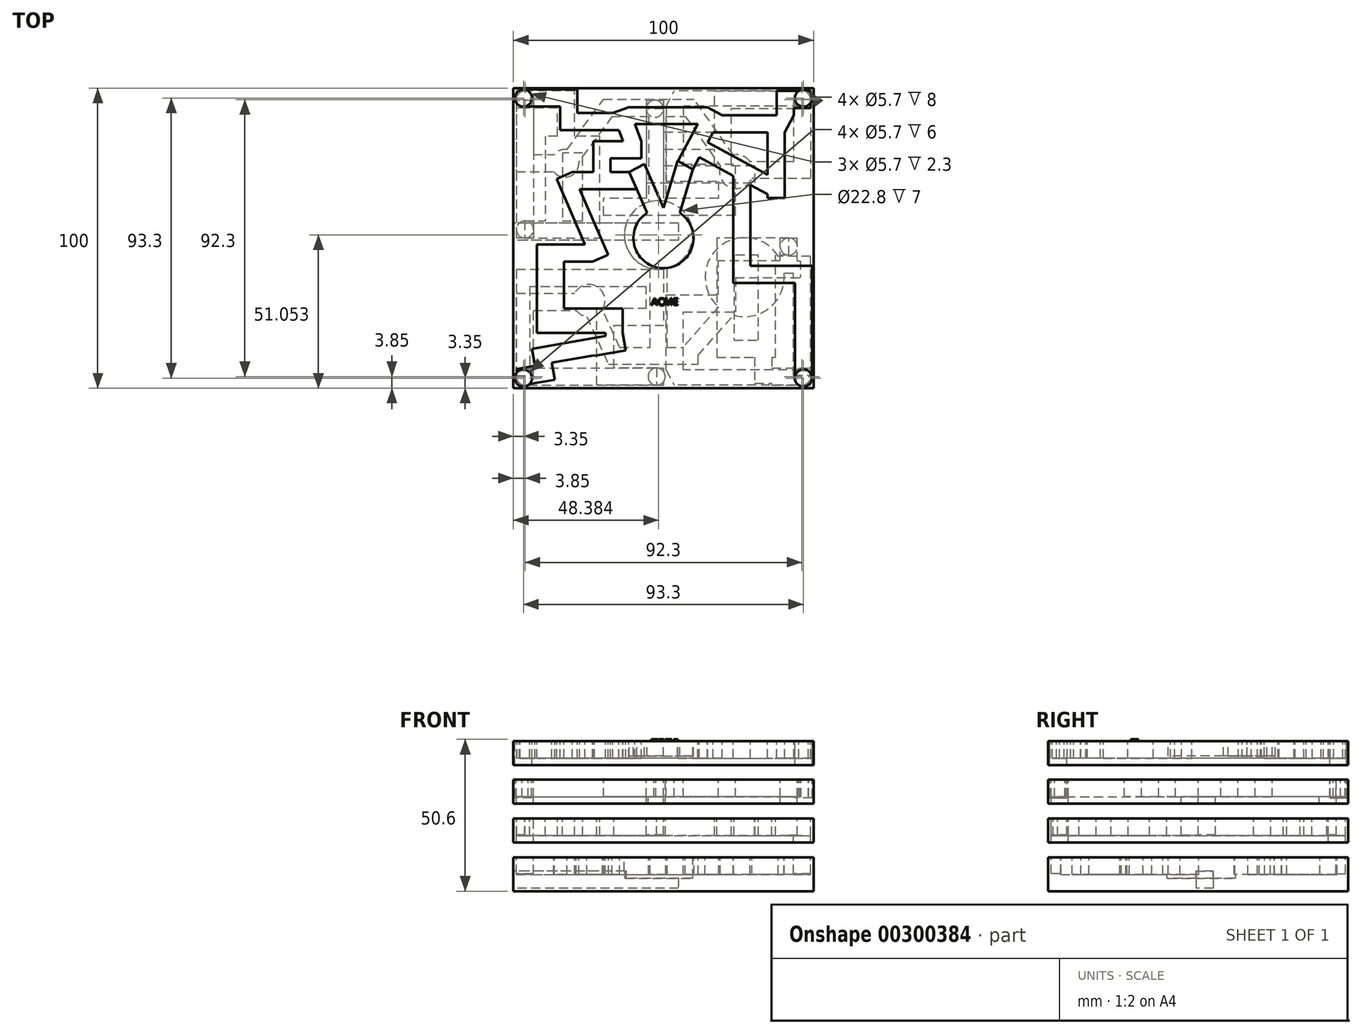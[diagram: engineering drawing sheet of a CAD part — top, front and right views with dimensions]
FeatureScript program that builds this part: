
annotation { "Feature Type Name" : "Feature", "Feature Type Description" : "" }
export const myFeature = defineFeature(function(context is Context, id is Id, definition is map)
    precondition{}
    {
        {
            var Q0;
            Q0=qCreatedBy(makeId("Top.planeOp"),FACE);
            var sketch = newSketch(context, id + "F0", { "sketchPlane" : qUnion([Q0])});
            skLineSegment(sketch, "E0.bottom", {"start": v(-50, 50) * mm, "end": v(50, 50) * mm});
            skLineSegment(sketch, "E0.top", {"start": v(-50, -50) * mm, "end": v(50, -50) * mm});
            skLineSegment(sketch, "E0.left", {"start": v(-50, 50) * mm, "end": v(-50, -50) * mm});
            skLineSegment(sketch, "E0.right", {"start": v(50, 50) * mm, "end": v(50, -50) * mm});
            skPoint(sketch, "E0.middle", {"position": v(0, 0) * mm});
            skSolve(sketch);
        }
        {
            var Q0;
            Q0=qSketchRegion(id+"F0",true);
            extrude(context, id + "F1", {"entities" : qUnion([Q0]), "oppositeDirection" : true, "depth" : 50 * mm});
        }
        {
            var Q0;
            Q0=makeQuery(id+"F1.opExtrude","CAP_FACE",FACE,{"disambiguationData":[OSD([sQuery(id+"F0.wireOp",EDGE,"E0.bottom"),sQuery(id+"F0.wireOp",EDGE,"E0.top"),sQuery(id+"F0.wireOp",EDGE,"E0.left"),sQuery(id+"F0.wireOp",EDGE,"E0.right")])],"isStart":true});
            var sketch = newSketch(context, id + "F2", { "sketchPlane" : qUnion([Q0])});
            skCircle(sketch, "E1", {"center": v(0, 0) * mm, "radius": 10 * mm});
            skSolve(sketch);
        }
        {
            var Q0;
            Q0=qSketchRegion(id+"F2",true);
            extrude(context, id + "F3", {"entities" : qUnion([Q0]), "operationType" : NewBodyOperationType.REMOVE, "oppositeDirection" : true, "depth" : 5 * mm});
        }
        {
            var Q0;
            Q0=makeQuery(id+"F1.opExtrude","CAP_FACE",FACE,{"disambiguationData":[OSD([sQuery(id+"F0.wireOp",EDGE,"E0.bottom"),sQuery(id+"F0.wireOp",EDGE,"E0.top"),sQuery(id+"F0.wireOp",EDGE,"E0.left"),sQuery(id+"F0.wireOp",EDGE,"E0.right")])],"isStart":true});
            var sketch = newSketch(context, id + "F4", { "sketchPlane" : qUnion([Q0])});
            skLineSegment(sketch, "E2", {"start": v(0, 10) * mm, "end": v(-6.36, 24.68) * mm});
            skLineSegment(sketch, "E3", {"start": v(0, 10) * mm, "end": v(4.66, 25.69) * mm});
            skLineSegment(sketch, "E4", {"start": v(4.66, 25.69) * mm, "end": v(9.78, 22.9) * mm});
            skLineSegment(sketch, "E5", {"start": v(9.78, 22.9) * mm, "end": v(5.46, 8.38) * mm});
            skLineSegment(sketch, "E6", {"start": v(5.46, 8.38) * mm, "end": v(0, 10) * mm});
            skLineSegment(sketch, "E7", {"start": v(-6.36, 24.68) * mm, "end": v(-11.36, 21.94) * mm});
            skLineSegment(sketch, "E8", {"start": v(-11.36, 21.94) * mm, "end": v(-5.46, 8.38) * mm});
            skLineSegment(sketch, "E9", {"start": v(-5.46, 8.38) * mm, "end": v(0, 10) * mm});
            skSolve(sketch);
        }
        {
            var Q0;
            Q0=qSketchRegion(id+"F4",true);
            extrude(context, id + "F5", {"entities" : qUnion([Q0]), "operationType" : NewBodyOperationType.REMOVE, "oppositeDirection" : true, "depth" : 5 * mm});
        }
        {
            var Q0;
            Q0=makeQuery(id+"F1.opExtrude","CAP_FACE",FACE,{"disambiguationData":[OSD([sQuery(id+"F0.wireOp",EDGE,"E0.bottom"),sQuery(id+"F0.wireOp",EDGE,"E0.top"),sQuery(id+"F0.wireOp",EDGE,"E0.left"),sQuery(id+"F0.wireOp",EDGE,"E0.right")])],"isStart":true});
            var sketch = newSketch(context, id + "F6", { "sketchPlane" : qUnion([Q0])});
            skLineSegment(sketch, "E10.bottom", {"start": v(-11.36, 21.94) * mm, "end": v(-30.36, 21.94) * mm});
            skLineSegment(sketch, "E10.top", {"start": v(-8.88, 16.24) * mm, "end": v(-27.88, 16.24) * mm});
            skLineSegment(sketch, "E10.left", {"start": v(-11.36, 21.94) * mm, "end": v(-8.88, 16.24) * mm});
            skLineSegment(sketch, "E10.right", {"start": v(-30.36, 21.94) * mm, "end": v(-27.88, 16.24) * mm});
            skLineSegment(sketch, "E11.bottom", {"start": v(-23.36, 21.94) * mm, "end": v(-17.66, 21.94) * mm});
            skLineSegment(sketch, "E11.top", {"start": v(-23.36, 32.25) * mm, "end": v(-17.66, 32.25) * mm});
            skLineSegment(sketch, "E11.left", {"start": v(-23.36, 21.94) * mm, "end": v(-23.36, 32.25) * mm});
            skLineSegment(sketch, "E11.right", {"start": v(-17.66, 21.94) * mm, "end": v(-17.66, 32.25) * mm});
            skLineSegment(sketch, "E12.bottom", {"start": v(-17.66, 32.25) * mm, "end": v(-7.41, 32.25) * mm});
            skLineSegment(sketch, "E12.top", {"start": v(-17.66, 26.55) * mm, "end": v(-7.41, 26.55) * mm});
            skLineSegment(sketch, "E12.left", {"start": v(-17.66, 32.25) * mm, "end": v(-17.66, 26.55) * mm});
            skLineSegment(sketch, "E12.right", {"start": v(-7.41, 32.25) * mm, "end": v(-7.41, 26.55) * mm});
            skLineSegment(sketch, "E13.bottom", {"start": v(-7.41, 32.25) * mm, "end": v(-12.77, 30.3) * mm});
            skLineSegment(sketch, "E13.top", {"start": v(-11.56, 43.65) * mm, "end": v(-16.92, 41.7) * mm});
            skLineSegment(sketch, "E13.left", {"start": v(-7.41, 32.25) * mm, "end": v(-11.56, 43.65) * mm});
            skLineSegment(sketch, "E13.right", {"start": v(-12.77, 30.3) * mm, "end": v(-16.92, 41.7) * mm});
            skLineSegment(sketch, "E14.bottom", {"start": v(-16.92, 41.7) * mm, "end": v(-31.14, 41.7) * mm});
            skLineSegment(sketch, "E14.top", {"start": v(-14.84, 36) * mm, "end": v(-29.06, 36) * mm});
            skLineSegment(sketch, "E14.left", {"start": v(-16.92, 41.7) * mm, "end": v(-14.84, 36) * mm});
            skLineSegment(sketch, "E14.right", {"start": v(-31.14, 41.7) * mm, "end": v(-29.06, 36) * mm});
            skLineSegment(sketch, "E15.bottom", {"start": v(-28.72, 36) * mm, "end": v(-34.42, 36) * mm});
            skLineSegment(sketch, "E15.top", {"start": v(-28.72, 49.5) * mm, "end": v(-34.42, 49.5) * mm});
            skLineSegment(sketch, "E15.left", {"start": v(-28.72, 36) * mm, "end": v(-28.72, 49.5) * mm});
            skLineSegment(sketch, "E15.right", {"start": v(-34.42, 36) * mm, "end": v(-34.42, 49.5) * mm});
            skLineSegment(sketch, "E16.bottom", {"start": v(-47.8, 49.5) * mm, "end": v(-34.42, 49.5) * mm});
            skLineSegment(sketch, "E16.top", {"start": v(-47.8, 43.8) * mm, "end": v(-34.42, 43.8) * mm});
            skLineSegment(sketch, "E16.left", {"start": v(-47.8, 49.5) * mm, "end": v(-47.8, 43.8) * mm});
            skLineSegment(sketch, "E16.right", {"start": v(-34.42, 49.5) * mm, "end": v(-34.42, 43.8) * mm});
            skLineSegment(sketch, "E17.bottom", {"start": v(-30.36, 21.94) * mm, "end": v(-35.59, 19.66) * mm});
            skLineSegment(sketch, "E17.top", {"start": v(-18.4, -5.57) * mm, "end": v(-23.62, -7.85) * mm});
            skLineSegment(sketch, "E17.left", {"start": v(-30.36, 21.94) * mm, "end": v(-18.4, -5.57) * mm});
            skLineSegment(sketch, "E17.right", {"start": v(-35.59, 19.66) * mm, "end": v(-23.62, -7.85) * mm});
            skLineSegment(sketch, "E18.bottom", {"start": v(-23.62, -7.85) * mm, "end": v(-42.16, -7.85) * mm});
            skLineSegment(sketch, "E18.top", {"start": v(-23.62, -2.15) * mm, "end": v(-42.16, -2.15) * mm});
            skLineSegment(sketch, "E18.left", {"start": v(-23.62, -7.85) * mm, "end": v(-23.62, -2.15) * mm});
            skLineSegment(sketch, "E18.right", {"start": v(-42.16, -7.85) * mm, "end": v(-42.16, -2.15) * mm});
            skLineSegment(sketch, "E19.bottom", {"start": v(-42.16, -7.85) * mm, "end": v(-33.16, -7.85) * mm});
            skLineSegment(sketch, "E19.top", {"start": v(-42.16, -31.6) * mm, "end": v(-33.16, -31.6) * mm});
            skLineSegment(sketch, "E19.left", {"start": v(-42.16, -7.85) * mm, "end": v(-42.16, -31.6) * mm});
            skLineSegment(sketch, "E19.right", {"start": v(-33.16, -7.85) * mm, "end": v(-33.16, -31.6) * mm});
            skLineSegment(sketch, "E20.bottom", {"start": v(-33.16, -23.52) * mm, "end": v(-13.61, -23.52) * mm});
            skLineSegment(sketch, "E20.top", {"start": v(-33.16, -31.6) * mm, "end": v(-13.61, -31.6) * mm});
            skLineSegment(sketch, "E20.left", {"start": v(-33.16, -23.52) * mm, "end": v(-33.16, -31.6) * mm});
            skLineSegment(sketch, "E20.right", {"start": v(-13.61, -23.52) * mm, "end": v(-13.61, -31.6) * mm});
            skLineSegment(sketch, "E21.bottom", {"start": v(-13.61, -31.6) * mm, "end": v(-24.04, -33.45) * mm});
            skLineSegment(sketch, "E21.top", {"start": v(-12.58, -37.43) * mm, "end": v(-23.02, -39.27) * mm});
            skLineSegment(sketch, "E21.left", {"start": v(-13.61, -31.6) * mm, "end": v(-12.58, -37.43) * mm});
            skLineSegment(sketch, "E21.right", {"start": v(-24.04, -33.45) * mm, "end": v(-23.02, -39.27) * mm});
            skLineSegment(sketch, "E22.bottom", {"start": v(-13.61, -31.6) * mm, "end": v(-19.31, -31.6) * mm});
            skLineSegment(sketch, "E22.top", {"start": v(-13.61, -32.61) * mm, "end": v(-19.31, -32.61) * mm});
            skLineSegment(sketch, "E22.left", {"start": v(-13.61, -31.6) * mm, "end": v(-13.61, -32.61) * mm});
            skLineSegment(sketch, "E22.right", {"start": v(-19.31, -31.6) * mm, "end": v(-19.31, -32.61) * mm});
            skLineSegment(sketch, "E23.bottom", {"start": v(-24.04, -33.45) * mm, "end": v(-43.78, -36.92) * mm});
            skLineSegment(sketch, "E23.top", {"start": v(-23.05, -39.06) * mm, "end": v(-42.79, -42.54) * mm});
            skLineSegment(sketch, "E23.left", {"start": v(-24.04, -33.45) * mm, "end": v(-23.05, -39.06) * mm});
            skLineSegment(sketch, "E23.right", {"start": v(-43.78, -36.92) * mm, "end": v(-42.79, -42.54) * mm});
            skLineSegment(sketch, "E24.bottom", {"start": v(-42.79, -42.54) * mm, "end": v(-37.17, -41.55) * mm});
            skLineSegment(sketch, "E24.top", {"start": v(-41.8, -48.15) * mm, "end": v(-36.18, -47.16) * mm});
            skLineSegment(sketch, "E24.left", {"start": v(-42.79, -42.54) * mm, "end": v(-41.8, -48.15) * mm});
            skLineSegment(sketch, "E24.right", {"start": v(-37.17, -41.55) * mm, "end": v(-36.18, -47.16) * mm});
            skLineSegment(sketch, "E25.bottom", {"start": v(-41.8, -48.15) * mm, "end": v(-47.94, -49.24) * mm});
            skLineSegment(sketch, "E25.top", {"start": v(-42.79, -42.54) * mm, "end": v(-48.93, -43.62) * mm});
            skLineSegment(sketch, "E25.left", {"start": v(-41.8, -48.15) * mm, "end": v(-42.79, -42.54) * mm});
            skLineSegment(sketch, "E25.right", {"start": v(-47.94, -49.24) * mm, "end": v(-48.93, -43.62) * mm});
            skLineSegment(sketch, "E26.bottom", {"start": v(9.78, 22.9) * mm, "end": v(19.57, 40.93) * mm});
            skLineSegment(sketch, "E26.top", {"start": v(4.77, 25.63) * mm, "end": v(14.56, 43.65) * mm});
            skLineSegment(sketch, "E26.left", {"start": v(9.78, 22.9) * mm, "end": v(4.77, 25.63) * mm});
            skLineSegment(sketch, "E26.right", {"start": v(19.57, 40.93) * mm, "end": v(14.56, 43.65) * mm});
            skPoint(sketch, "E27.oppositeSnap0", {"position": v(-9.49, 37.95) * mm});
            skLineSegment(sketch, "E27.bottom", {"start": v(14.56, 43.65) * mm, "end": v(-11.56, 43.65) * mm});
            skLineSegment(sketch, "E27.top", {"start": v(11.47, 37.95) * mm, "end": v(-9.49, 37.95) * mm});
            skLineSegment(sketch, "E27.left", {"start": v(14.56, 43.65) * mm, "end": v(11.47, 37.95) * mm});
            skLineSegment(sketch, "E27.right", {"start": v(-11.56, 43.65) * mm, "end": v(-9.49, 37.95) * mm});
            skLineSegment(sketch, "E28.bottom", {"start": v(19.57, 40.93) * mm, "end": v(43.44, 40.93) * mm});
            skLineSegment(sketch, "E28.top", {"start": v(16.47, 35.23) * mm, "end": v(40.35, 35.23) * mm});
            skLineSegment(sketch, "E28.left", {"start": v(19.57, 40.93) * mm, "end": v(16.47, 35.23) * mm});
            skLineSegment(sketch, "E28.right", {"start": v(43.44, 40.93) * mm, "end": v(40.35, 35.23) * mm});
            skLineSegment(sketch, "E29.bottom", {"start": v(40.35, 35.23) * mm, "end": v(34.65, 35.23) * mm});
            skLineSegment(sketch, "E29.top", {"start": v(40.35, 13.41) * mm, "end": v(34.65, 13.41) * mm});
            skLineSegment(sketch, "E29.left", {"start": v(40.35, 35.23) * mm, "end": v(40.35, 13.41) * mm});
            skLineSegment(sketch, "E29.right", {"start": v(34.65, 35.23) * mm, "end": v(34.65, 13.41) * mm});
            skLineSegment(sketch, "E30.bottom", {"start": v(14.68, 31.92) * mm, "end": v(37.37, 19.6) * mm});
            skLineSegment(sketch, "E30.top", {"start": v(11.96, 26.9) * mm, "end": v(34.65, 14.59) * mm});
            skLineSegment(sketch, "E30.left", {"start": v(14.68, 31.92) * mm, "end": v(11.96, 26.9) * mm});
            skLineSegment(sketch, "E30.right", {"start": v(37.37, 19.6) * mm, "end": v(34.65, 14.59) * mm});
            skLineSegment(sketch, "E31.bottom", {"start": v(23.3, 20.75) * mm, "end": v(29, 17.65) * mm});
            skLineSegment(sketch, "E31.top", {"start": v(23.3, -14.96) * mm, "end": v(29, -14.96) * mm});
            skLineSegment(sketch, "E31.left", {"start": v(23.3, 20.75) * mm, "end": v(23.3, -14.96) * mm});
            skLineSegment(sketch, "E31.right", {"start": v(29, 17.65) * mm, "end": v(29, -14.96) * mm});
            skLineSegment(sketch, "E32.bottom", {"start": v(29, -14.96) * mm, "end": v(29, -9.26) * mm});
            skLineSegment(sketch, "E32.top", {"start": v(49.5, -14.96) * mm, "end": v(49.5, -9.26) * mm});
            skLineSegment(sketch, "E32.left", {"start": v(29, -14.96) * mm, "end": v(49.5, -14.96) * mm});
            skLineSegment(sketch, "E32.right", {"start": v(29, -9.26) * mm, "end": v(49.5, -9.26) * mm});
            skLineSegment(sketch, "E33.bottom", {"start": v(43.8, -14.96) * mm, "end": v(49.5, -14.96) * mm});
            skLineSegment(sketch, "E33.top", {"start": v(43.8, -46.22) * mm, "end": v(49.5, -46.22) * mm});
            skLineSegment(sketch, "E33.left", {"start": v(43.8, -14.96) * mm, "end": v(43.8, -46.22) * mm});
            skLineSegment(sketch, "E33.right", {"start": v(49.5, -14.96) * mm, "end": v(49.5, -46.22) * mm});
            skLineSegment(sketch, "E34.bottom", {"start": v(43.44, 40.93) * mm, "end": v(37.74, 40.93) * mm});
            skLineSegment(sketch, "E34.top", {"start": v(43.44, 49.03) * mm, "end": v(37.74, 49.03) * mm});
            skLineSegment(sketch, "E34.left", {"start": v(43.44, 40.93) * mm, "end": v(43.44, 49.03) * mm});
            skLineSegment(sketch, "E34.right", {"start": v(37.74, 40.93) * mm, "end": v(37.74, 49.03) * mm});
            skLineSegment(sketch, "E35.bottom", {"start": v(43.44, 49.03) * mm, "end": v(49.05, 49.03) * mm});
            skLineSegment(sketch, "E35.top", {"start": v(43.44, 43.33) * mm, "end": v(49.05, 43.33) * mm});
            skLineSegment(sketch, "E35.left", {"start": v(43.44, 49.03) * mm, "end": v(43.44, 43.33) * mm});
            skLineSegment(sketch, "E35.right", {"start": v(49.05, 49.03) * mm, "end": v(49.05, 43.33) * mm});
            skSolve(sketch);
        }
        {
            var Q0;
            {var subQ14=sQuery(id+"F6.wireOp",EDGE,"E10.top");Q0=makeQuery(id+"F6.imprint","IMPRINT",FACE,{"disambiguationData":[TD([[makeQuery(id+"F6.imprint","IMPRINT",EDGE,{"derivedFrom":subQ14}),1.0]])]});}
            var sketch = newSketch(context, id + "F7", { "sketchPlane" : qUnion([Q0])});
            skCircle(sketch, "E36", {"center": v(-46.65, 46.65) * mm, "radius": 2.85 * mm});
            skCircle(sketch, "E37", {"center": v(-46.65, -46.65) * mm, "radius": 2.85 * mm});
            skCircle(sketch, "E38", {"center": v(46.65, -46.65) * mm, "radius": 2.85 * mm});
            skCircle(sketch, "E39", {"center": v(46.65, 46.65) * mm, "radius": 2.85 * mm});
            skSolve(sketch);
        }
        {
            var Q0;
            Q0=qSketchRegion(id+"F6",true);
            extrude(context, id + "F8", {"entities" : qUnion([Q0]), "operationType" : NewBodyOperationType.REMOVE, "oppositeDirection" : true, "depth" : 5.7 * mm});
        }
        {
            var Q0;
            {var subQ16=sQuery(id+"F6.wireOp",EDGE,"E10.top");Q0=makeQuery(id+"F7.imprint","IMPRINT",FACE,{"disambiguationData":[TD([[makeQuery(id+"F7.imprint","IMPRINT",EDGE,{"derivedFrom":makeQuery(id+"F6.imprint","IMPRINT",EDGE,{"derivedFrom":subQ16})}),1.0]])]});}
            var sketch = newSketch(context, id + "F9", { "sketchPlane" : qUnion([Q0])});
            skText(sketch, "E40", { "text": "ACME", "fontName": "OpenSans-Regular.ttf"});
            const initialGuessF9  = {"E40": [-0.004, -0.02238, 1, 0, 0.00238]};
            skSetInitialGuess(sketch, initialGuessF9);
            skSolve(sketch);
        }
        {
            var Q0;
            Q0=qSketchRegion(id+"F9",true);
            extrude(context, id + "F10", {"entities" : qUnion([Q0]), "operationType" : NewBodyOperationType.ADD, "depth" : 0.6 * mm});
        }
        {
            var Q0;
            Q0=makeQuery(id+"F1.opExtrude","SWEPT_FACE",FACE,{"disambiguationData":[OSD([sQuery(id+"F0.wireOp",EDGE,"E0.top")])]});
            var sketch = newSketch(context, id + "F11", { "sketchPlane" : qUnion([Q0])});
            skLineSegment(sketch, "E41.bottom", {"start": v(-50, -8) * mm, "end": v(50, -8) * mm});
            skLineSegment(sketch, "E41.top", {"start": v(-50, -12.9) * mm, "end": v(50, -12.9) * mm});
            skLineSegment(sketch, "E41.left", {"start": v(-50, -8) * mm, "end": v(-50, -12.9) * mm});
            skLineSegment(sketch, "E41.right", {"start": v(50, -8) * mm, "end": v(50, -12.9) * mm});
            skSolve(sketch);
        }
        {
            var Q0;
            Q0=qSketchRegion(id+"F11",true);
            extrude(context, id + "F12", {"entities" : qUnion([Q0]), "operationType" : NewBodyOperationType.REMOVE, "endBound" : BoundingType.THROUGH_ALL, "oppositeDirection" : true, "depth" : 25 * mm});
        }
        {
            var Q0;
            Q0=makeQuery(id+"F12.boolean.opBoolean","COPY",FACE,{"derivedFrom":makeQuery(id+"F12.opExtrude","SWEPT_FACE",FACE,{"disambiguationData":[OSD([sQuery(id+"F11.wireOp",EDGE,"E41.top")])]})});
            var sketch = newSketch(context, id + "F13", { "sketchPlane" : qUnion([Q0])});
            skCircle(sketch, "E42", {"center": v(-46.65, -46.65) * mm, "radius": 2.85 * mm});
            skCircle(sketch, "E43.MirrorC", {"center": v(46.65, -46.65) * mm, "radius": 2.85 * mm});
            skCircle(sketch, "E44.MirrorC", {"center": v(-46.65, 46.65) * mm, "radius": 2.85 * mm});
            skCircle(sketch, "E45.MirrorC", {"center": v(46.65, 46.65) * mm, "radius": 2.85 * mm});
            skSolve(sketch);
        }
        {
            var Q0;
            Q0=qSketchRegion(id+"F13",true);
            extrude(context, id + "F14", {"entities" : qUnion([Q0]), "operationType" : NewBodyOperationType.REMOVE, "oppositeDirection" : true, "depth" : 6 * mm});
        }
        {
            var Q0;
            Q0=makeQuery(id+"F12.boolean.opBoolean","COPY",FACE,{"derivedFrom":makeQuery(id+"F12.opExtrude","SWEPT_FACE",FACE,{"disambiguationData":[OSD([sQuery(id+"F11.wireOp",EDGE,"E41.top")])]})});
            var sketch = newSketch(context, id + "F15", { "sketchPlane" : qUnion([Q0])});
            skLineSegment(sketch, "E46.bottom", {"start": v(45.8, -43.93) * mm, "end": v(0.93, -43.93) * mm});
            skLineSegment(sketch, "E46.top", {"start": v(48.4, -49) * mm, "end": v(3.54, -49) * mm});
            skLineSegment(sketch, "E46.left", {"start": v(45.8, -43.93) * mm, "end": v(48.4, -49) * mm});
            skLineSegment(sketch, "E46.right", {"start": v(0.93, -43.93) * mm, "end": v(3.54, -49) * mm});
            skLineSegment(sketch, "E47.MirrorCS", {"start": v(45.8, 43.93) * mm, "end": v(0.93, 43.93) * mm});
            skLineSegment(sketch, "E48.MirrorCS", {"start": v(45.8, 43.93) * mm, "end": v(48.4, 49) * mm});
            skLineSegment(sketch, "E49.MirrorCS", {"start": v(48.4, 49) * mm, "end": v(3.54, 49) * mm});
            skLineSegment(sketch, "E50.MirrorCS", {"start": v(0.93, 43.93) * mm, "end": v(3.54, 49) * mm});
            skLineSegment(sketch, "E51.bottom", {"start": v(0.93, -43.93) * mm, "end": v(6.63, -43.93) * mm});
            skLineSegment(sketch, "E51.top", {"start": v(0.93, -18.93) * mm, "end": v(6.63, -18.93) * mm});
            skLineSegment(sketch, "E51.left", {"start": v(0.93, -43.93) * mm, "end": v(0.93, -18.93) * mm});
            skLineSegment(sketch, "E51.right", {"start": v(6.63, -43.93) * mm, "end": v(6.63, -18.93) * mm});
            skLineSegment(sketch, "E52.bottom", {"start": v(6.63, -18.93) * mm, "end": v(23.97, -18.93) * mm});
            skLineSegment(sketch, "E52.top", {"start": v(6.63, -24.63) * mm, "end": v(23.97, -24.63) * mm});
            skLineSegment(sketch, "E52.left", {"start": v(6.63, -18.93) * mm, "end": v(6.63, -24.63) * mm});
            skLineSegment(sketch, "E52.right", {"start": v(23.97, -18.93) * mm, "end": v(23.97, -24.63) * mm});
            skLineSegment(sketch, "E53.MirrorCS", {"start": v(6.63, 18.93) * mm, "end": v(23.97, 18.93) * mm});
            skLineSegment(sketch, "E54.MirrorCS", {"start": v(6.63, 24.63) * mm, "end": v(23.97, 24.63) * mm});
            skLineSegment(sketch, "E55.MirrorCS", {"start": v(23.97, 18.93) * mm, "end": v(23.97, 24.63) * mm});
            skLineSegment(sketch, "E56.MirrorCS", {"start": v(6.63, 43.93) * mm, "end": v(6.63, 18.93) * mm});
            skLineSegment(sketch, "E57.MirrorCS", {"start": v(0.93, 43.93) * mm, "end": v(0.93, 18.93) * mm});
            skLineSegment(sketch, "E58.MirrorCS", {"start": v(0.93, 18.93) * mm, "end": v(6.63, 18.93) * mm});
            skLineSegment(sketch, "E59.MirrorCS", {"start": v(0.93, 43.93) * mm, "end": v(6.63, 43.93) * mm});
            skLineSegment(sketch, "E60.bottom", {"start": v(23.97, -18.93) * mm, "end": v(18.27, -18.93) * mm});
            skLineSegment(sketch, "E60.top", {"start": v(23.97, -7.53) * mm, "end": v(18.27, -7.53) * mm});
            skLineSegment(sketch, "E60.left", {"start": v(23.97, -18.93) * mm, "end": v(23.97, -7.53) * mm});
            skLineSegment(sketch, "E60.right", {"start": v(18.27, -18.93) * mm, "end": v(18.27, -7.53) * mm});
            skLineSegment(sketch, "E61.left", {"start": v(18.27, -7.53) * mm, "end": v(18.27, -13.23) * mm});
            skLineSegment(sketch, "E62.MirrorCS", {"start": v(18.27, 18.93) * mm, "end": v(18.27, 7.53) * mm});
            skLineSegment(sketch, "E63.MirrorCS", {"start": v(23.97, 18.93) * mm, "end": v(23.97, 7.53) * mm});
            skLineSegment(sketch, "E64.MirrorCS", {"start": v(23.97, 7.53) * mm, "end": v(18.27, 7.53) * mm});
            skLineSegment(sketch, "E65.MirrorCS", {"start": v(18.27, 7.53) * mm, "end": v(-19.9, 7.53) * mm});
            skLineSegment(sketch, "E66.MirrorCS", {"start": v(18.27, 13.23) * mm, "end": v(-19.9, 13.23) * mm});
            skLineSegment(sketch, "E67.MirrorCS", {"start": v(0, 45.93) * mm, "end": v(-5.7, 45.93) * mm});
            skLineSegment(sketch, "E68.MirrorCS", {"start": v(-5.7, 45.93) * mm, "end": v(-5.7, 8.83) * mm});
            skLineSegment(sketch, "E69.MirrorCS", {"start": v(0, 45.93) * mm, "end": v(0, 8.83) * mm});
            skLineSegment(sketch, "E70.MirrorCS", {"start": v(0, 8.83) * mm, "end": v(-5.7, 8.83) * mm});
            skPoint(sketch, "E71.oppositeSnap0", {"position": v(23.97, -13.23) * mm});
            skLineSegment(sketch, "E71.bottom", {"start": v(23.97, -7.53) * mm, "end": v(45.56, -7.53) * mm});
            skLineSegment(sketch, "E71.top", {"start": v(23.97, -13.23) * mm, "end": v(45.56, -13.23) * mm});
            skLineSegment(sketch, "E71.left", {"start": v(23.97, -7.53) * mm, "end": v(23.97, -13.23) * mm});
            skLineSegment(sketch, "E71.right", {"start": v(45.56, -7.53) * mm, "end": v(45.56, -13.23) * mm});
            skLineSegment(sketch, "E72.bottom", {"start": v(38.91, -7.53) * mm, "end": v(44.61, -7.53) * mm});
            skLineSegment(sketch, "E72.top", {"start": v(38.91, 0) * mm, "end": v(44.61, 0) * mm});
            skLineSegment(sketch, "E72.left", {"start": v(38.91, -7.53) * mm, "end": v(38.91, 0) * mm});
            skLineSegment(sketch, "E72.right", {"start": v(44.61, -7.53) * mm, "end": v(44.61, 0) * mm});
            skLineSegment(sketch, "E73", {"start": v(-19.9, 7.53) * mm, "end": v(-19.9, 13.23) * mm});
            skPoint(sketch, "E74.oppositeSnap0", {"position": v(0, -50) * mm});
            skLineSegment(sketch, "E74.bottom", {"start": v(-46.46, -43.3) * mm, "end": v(0, -43.3) * mm});
            skLineSegment(sketch, "E74.top", {"start": v(-46.46, -49) * mm, "end": v(0, -49) * mm});
            skLineSegment(sketch, "E74.left", {"start": v(-46.46, -43.3) * mm, "end": v(-46.46, -49) * mm});
            skLineSegment(sketch, "E74.right", {"start": v(0, -43.3) * mm, "end": v(0, -49) * mm});
            skLineSegment(sketch, "E75.bottom", {"start": v(-43.3, 47.45) * mm, "end": v(-49, 47.45) * mm});
            skLineSegment(sketch, "E75.top", {"start": v(-43.3, 0) * mm, "end": v(-49, 0) * mm});
            skLineSegment(sketch, "E75.left", {"start": v(-43.3, 47.45) * mm, "end": v(-43.3, 0) * mm});
            skLineSegment(sketch, "E75.right", {"start": v(-49, 47.45) * mm, "end": v(-49, 0) * mm});
            skLineSegment(sketch, "E76", {"start": v(-46.46, -43.3) * mm, "end": v(-47.15, -43.3) * mm});
            skLineSegment(sketch, "E77", {"start": v(-47.15, -43.3) * mm, "end": v(-47.15, -43.84) * mm});
            skLineSegment(sketch, "E78", {"start": v(-47.15, -43.84) * mm, "end": v(-46.46, -43.8) * mm});
            skLineSegment(sketch, "E79", {"start": v(44.66, -49) * mm, "end": v(45.6, -49.3) * mm});
            skLineSegment(sketch, "E80", {"start": v(45.6, -49.3) * mm, "end": v(45.6, -49) * mm});
            skLineSegment(sketch, "E81", {"start": v(44.99, -43.93) * mm, "end": v(46.24, -44.8) * mm});
            skSolve(sketch);
        }
        {
            var Q0;
            Q0=qSketchRegion(id+"F15",true);
            var Q1;
            Q1=qSketchRegion(id+"F17",true);
            extrude(context, id + "F16", {"entities" : qUnion([Q0, Q1]), "operationType" : NewBodyOperationType.REMOVE, "oppositeDirection" : true, "depth" : 5.7 * mm});
        }
        {
            var Q0;
            Q0=makeQuery(id+"F12.boolean.opBoolean","COPY",FACE,{"derivedFrom":makeQuery(id+"F12.opExtrude","SWEPT_FACE",FACE,{"disambiguationData":[OSD([sQuery(id+"F11.wireOp",EDGE,"E41.top")])]})});
            var sketch = newSketch(context, id + "F17", { "sketchPlane" : qUnion([Q0])});
            skCircle(sketch, "E82", {"center": v(-2.26, -46.15) * mm, "radius": 2.85 * mm});
            skPoint(sketch, "E82.first.point", {"position": v(0, -43.3) * mm});
            skPoint(sketch, "E82.second.point", {"position": v(-2.26, -49) * mm});
            skPoint(sketch, "E82.third.point", {"position": v(-2.26, -43.3) * mm});
            skCircle(sketch, "E83", {"center": v(41.76, -2.85) * mm, "radius": 2.85 * mm});
            skCircle(sketch, "E84", {"center": v(-46.15, 2.85) * mm, "radius": 2.85 * mm});
            skPoint(sketch, "E84.first.point", {"position": v(-43.3, 2.85) * mm});
            skPoint(sketch, "E84.second.point", {"position": v(-46.15, 0) * mm});
            skPoint(sketch, "E84.third.point", {"position": v(-49, 2.85) * mm});
            skCircle(sketch, "E85", {"center": v(-2.85, 43.1) * mm, "radius": 2.85 * mm});
            skPoint(sketch, "E85.first.point", {"position": v(0, 43.1) * mm});
            skPoint(sketch, "E85.second.point", {"position": v(-5.7, 43.1) * mm});
            skPoint(sketch, "E85.third.point", {"position": v(-3.16, 45.93) * mm});
            skSolve(sketch);
        }
        {
            var Q0;
            {var subQ2=sQuery(id+"F0.wireOp",EDGE,"E0.top");Q0=makeQuery(id+"F12.boolean.opBoolean","SPLIT",FACE,{"disambiguationData":[TD([makeQuery(id+"F12.opExtrude","SWEPT_FACE",FACE,{"disambiguationData":[OSD([sQuery(id+"F11.wireOp",EDGE,"E41.top")])]})])],"derivedFrom":makeQuery(id+"F1.opExtrude","SWEPT_FACE",FACE,{"disambiguationData":[OSD([subQ2])]})});}
            var sketch = newSketch(context, id + "F18", { "sketchPlane" : qUnion([Q0])});
            skLineSegment(sketch, "E86.bottom", {"start": v(-50, -12.9) * mm, "end": v(50, -12.9) * mm});
            skLineSegment(sketch, "E86.top", {"start": v(-50, -20.9) * mm, "end": v(50, -20.9) * mm});
            skLineSegment(sketch, "E86.left", {"start": v(-50, -12.9) * mm, "end": v(-50, -20.9) * mm});
            skLineSegment(sketch, "E86.right", {"start": v(50, -12.9) * mm, "end": v(50, -20.9) * mm});
            skSolve(sketch);
        }
        {
            var Q0;
            {var subQ0=sQuery(id+"F18.wireOp",EDGE,"E86.top");Q0=makeQuery(id+"F18.imprint","IMPRINT",FACE,{"disambiguationData":[TD([[makeQuery(id+"F18.imprint","IMPRINT",EDGE,{"derivedFrom":subQ0}),-1.0]])]});}
            var sketch = newSketch(context, id + "F19", { "sketchPlane" : qUnion([Q0])});
            skLineSegment(sketch, "E87.bottom", {"start": v(-50, -20.84) * mm, "end": v(50, -20.84) * mm});
            skLineSegment(sketch, "E87.top", {"start": v(-50, -25.8) * mm, "end": v(50, -25.8) * mm});
            skLineSegment(sketch, "E87.left", {"start": v(-50, -20.84) * mm, "end": v(-50, -25.8) * mm});
            skLineSegment(sketch, "E87.right", {"start": v(50, -20.84) * mm, "end": v(50, -25.8) * mm});
            skSolve(sketch);
        }
        {
            var Q0;
            Q0=qSketchRegion(id+"F17",true);
            extrude(context, id + "F20", {"entities" : qUnion([Q0]), "operationType" : NewBodyOperationType.REMOVE, "oppositeDirection" : true, "depth" : 18.4 * mm});
        }
        {
            var Q0;
            Q0=qSketchRegion(id+"F19",true);
            extrude(context, id + "F21", {"entities" : qUnion([Q0]), "operationType" : NewBodyOperationType.REMOVE, "endBound" : BoundingType.THROUGH_ALL, "oppositeDirection" : true, "depth" : 25 * mm});
        }
        {
            var Q0;
            Q0=makeQuery(id+"F21.boolean.opBoolean","COPY",FACE,{"derivedFrom":makeQuery(id+"F21.opExtrude","SWEPT_FACE",FACE,{"disambiguationData":[OSD([sQuery(id+"F19.wireOp",EDGE,"E87.top")])]})});
            var sketch = newSketch(context, id + "F22", { "sketchPlane" : qUnion([Q0])});
            skLineSegment(sketch, "E88.bottom", {"start": v(-2.28, -43.3) * mm, "end": v(-22.26, -43.3) * mm});
            skLineSegment(sketch, "E88.top", {"start": v(-2.28, -49) * mm, "end": v(-22.26, -49) * mm});
            skLineSegment(sketch, "E88.left", {"start": v(-2.28, -43.3) * mm, "end": v(-2.28, -49) * mm});
            skLineSegment(sketch, "E88.right", {"start": v(-22.26, -43.3) * mm, "end": v(-22.26, -49) * mm});
            skLineSegment(sketch, "E89.bottom", {"start": v(-22.26, -43.3) * mm, "end": v(-16.56, -43.3) * mm});
            skLineSegment(sketch, "E89.top", {"start": v(-22.26, -23.37) * mm, "end": v(-16.56, -23.37) * mm});
            skLineSegment(sketch, "E89.left", {"start": v(-22.26, -43.3) * mm, "end": v(-22.26, -23.37) * mm});
            skLineSegment(sketch, "E89.right", {"start": v(-16.56, -43.3) * mm, "end": v(-16.56, -23.37) * mm});
            skLineSegment(sketch, "E90.bottom", {"start": v(-16.56, -23.37) * mm, "end": v(0, -23.37) * mm});
            skLineSegment(sketch, "E90.top", {"start": v(-16.56, -29.07) * mm, "end": v(0, -29.07) * mm});
            skLineSegment(sketch, "E90.left", {"start": v(-16.56, -23.37) * mm, "end": v(-16.56, -29.07) * mm});
            skLineSegment(sketch, "E90.right", {"start": v(0, -23.37) * mm, "end": v(0, -29.07) * mm});
            skLineSegment(sketch, "E91.bottom", {"start": v(0, -23.37) * mm, "end": v(-5.7, -23.37) * mm});
            skLineSegment(sketch, "E91.top", {"start": v(0, -10.57) * mm, "end": v(-5.7, -10.57) * mm});
            skLineSegment(sketch, "E91.left", {"start": v(0, -23.37) * mm, "end": v(0, -10.57) * mm});
            skLineSegment(sketch, "E91.right", {"start": v(-5.7, -23.37) * mm, "end": v(-5.7, -10.57) * mm});
            skLineSegment(sketch, "E92.bottom", {"start": v(-5.7, -10.57) * mm, "end": v(-49, -10.57) * mm});
            skLineSegment(sketch, "E92.top", {"start": v(-5.7, -16.27) * mm, "end": v(-49, -16.27) * mm});
            skLineSegment(sketch, "E92.left", {"start": v(-5.7, -10.57) * mm, "end": v(-5.7, -16.27) * mm});
            skLineSegment(sketch, "E92.right", {"start": v(-49, -10.57) * mm, "end": v(-49, -16.27) * mm});
            skLineSegment(sketch, "E93.bottom", {"start": v(-49, -16.27) * mm, "end": v(-44.54, -16.27) * mm});
            skLineSegment(sketch, "E93.top", {"start": v(-49, -46.88) * mm, "end": v(-44.54, -46.88) * mm});
            skLineSegment(sketch, "E93.left", {"start": v(-49, -16.27) * mm, "end": v(-49, -46.88) * mm});
            skLineSegment(sketch, "E93.right", {"start": v(-44.54, -16.27) * mm, "end": v(-44.54, -46.88) * mm});
            skLineSegment(sketch, "E94.bottom", {"start": v(41.76, -5.7) * mm, "end": v(17.8, -5.7) * mm});
            skLineSegment(sketch, "E94.top", {"start": v(41.76, 0) * mm, "end": v(17.8, 0) * mm});
            skLineSegment(sketch, "E94.left", {"start": v(41.76, -5.7) * mm, "end": v(41.76, 0) * mm});
            skLineSegment(sketch, "E94.right", {"start": v(17.8, -5.7) * mm, "end": v(17.8, 0) * mm});
            skLineSegment(sketch, "E95.bottom", {"start": v(17.8, -5.7) * mm, "end": v(23.5, -5.7) * mm});
            skLineSegment(sketch, "E95.top", {"start": v(17.8, -39.76) * mm, "end": v(23.5, -39.76) * mm});
            skLineSegment(sketch, "E95.left", {"start": v(17.8, -5.7) * mm, "end": v(17.8, -39.76) * mm});
            skLineSegment(sketch, "E95.right", {"start": v(23.5, -5.7) * mm, "end": v(23.5, -39.76) * mm});
            skLineSegment(sketch, "E96.bottom", {"start": v(23.5, -39.76) * mm, "end": v(37.34, -39.76) * mm});
            skLineSegment(sketch, "E96.top", {"start": v(23.5, -34.06) * mm, "end": v(37.34, -34.06) * mm});
            skLineSegment(sketch, "E96.left", {"start": v(23.5, -39.76) * mm, "end": v(23.5, -34.06) * mm});
            skLineSegment(sketch, "E96.right", {"start": v(37.34, -39.76) * mm, "end": v(37.34, -34.06) * mm});
            skLineSegment(sketch, "E97.bottom", {"start": v(30.42, -39.76) * mm, "end": v(36.12, -39.76) * mm});
            skLineSegment(sketch, "E97.top", {"start": v(30.42, -48.3) * mm, "end": v(36.12, -48.3) * mm});
            skLineSegment(sketch, "E97.left", {"start": v(30.42, -39.76) * mm, "end": v(30.42, -48.3) * mm});
            skLineSegment(sketch, "E97.right", {"start": v(36.12, -39.76) * mm, "end": v(36.12, -48.3) * mm});
            skLineSegment(sketch, "E98.bottom", {"start": v(37.34, -34.06) * mm, "end": v(31.64, -34.06) * mm});
            skLineSegment(sketch, "E98.top", {"start": v(37.34, -5.7) * mm, "end": v(31.64, -5.7) * mm});
            skLineSegment(sketch, "E98.left", {"start": v(37.34, -34.06) * mm, "end": v(37.34, -5.7) * mm});
            skLineSegment(sketch, "E98.right", {"start": v(31.64, -34.06) * mm, "end": v(31.64, -5.7) * mm});
            skLineSegment(sketch, "E99.bottom", {"start": v(36.12, -49) * mm, "end": v(49, -49) * mm});
            skLineSegment(sketch, "E99.top", {"start": v(36.12, -43.3) * mm, "end": v(49, -43.3) * mm});
            skLineSegment(sketch, "E99.left", {"start": v(36.12, -49) * mm, "end": v(36.12, -43.3) * mm});
            skLineSegment(sketch, "E99.right", {"start": v(49, -49) * mm, "end": v(49, -43.3) * mm});
            skPoint(sketch, "E100.firstSnap0", {"position": v(0, 50) * mm});
            skLineSegment(sketch, "E100.bottom", {"start": v(0, 43.1) * mm, "end": v(-5.68, 43.1) * mm});
            skLineSegment(sketch, "E100.top", {"start": v(0, 37.9) * mm, "end": v(-5.68, 37.9) * mm});
            skLineSegment(sketch, "E100.left", {"start": v(0, 43.1) * mm, "end": v(0, 37.9) * mm});
            skLineSegment(sketch, "E100.right", {"start": v(-5.68, 43.1) * mm, "end": v(-5.68, 37.9) * mm});
            skLineSegment(sketch, "E101.bottom", {"start": v(0, 37.9) * mm, "end": v(-5.7, 37.9) * mm});
            skLineSegment(sketch, "E101.top", {"start": v(0, 18.47) * mm, "end": v(-5.7, 18.47) * mm});
            skLineSegment(sketch, "E101.left", {"start": v(0, 37.9) * mm, "end": v(0, 18.47) * mm});
            skLineSegment(sketch, "E101.right", {"start": v(-5.7, 37.9) * mm, "end": v(-5.7, 18.47) * mm});
            skLineSegment(sketch, "E102.bottom", {"start": v(0, 18.47) * mm, "end": v(30.48, 18.47) * mm});
            skLineSegment(sketch, "E102.top", {"start": v(0, 24.17) * mm, "end": v(30.48, 24.17) * mm});
            skLineSegment(sketch, "E102.left", {"start": v(0, 18.47) * mm, "end": v(0, 24.17) * mm});
            skLineSegment(sketch, "E102.right", {"start": v(30.48, 18.47) * mm, "end": v(30.48, 24.17) * mm});
            skLineSegment(sketch, "E103.bottom", {"start": v(22.67, 24.17) * mm, "end": v(16.97, 24.17) * mm});
            skLineSegment(sketch, "E103.top", {"start": v(22.67, 49) * mm, "end": v(16.97, 49) * mm});
            skLineSegment(sketch, "E103.left", {"start": v(22.67, 24.17) * mm, "end": v(22.67, 49) * mm});
            skLineSegment(sketch, "E103.right", {"start": v(16.97, 24.17) * mm, "end": v(16.97, 49) * mm});
            skLineSegment(sketch, "E104.bottom", {"start": v(16.97, 29.49) * mm, "end": v(0, 29.49) * mm});
            skLineSegment(sketch, "E104.top", {"start": v(16.97, 35.19) * mm, "end": v(0, 35.19) * mm});
            skLineSegment(sketch, "E104.left", {"start": v(16.97, 29.49) * mm, "end": v(16.97, 35.19) * mm});
            skLineSegment(sketch, "E104.right", {"start": v(0, 29.49) * mm, "end": v(0, 35.19) * mm});
            skLineSegment(sketch, "E105.bottom", {"start": v(22.67, 49) * mm, "end": v(49, 49) * mm});
            skLineSegment(sketch, "E105.top", {"start": v(22.67, 43.25) * mm, "end": v(49, 43.25) * mm});
            skLineSegment(sketch, "E105.left", {"start": v(22.67, 49) * mm, "end": v(22.67, 43.25) * mm});
            skLineSegment(sketch, "E105.right", {"start": v(49, 49) * mm, "end": v(49, 43.25) * mm});
            skLineSegment(sketch, "E106.bottom", {"start": v(-46.2, 5.7) * mm, "end": v(-21.16, 5.7) * mm});
            skLineSegment(sketch, "E106.top", {"start": v(-46.2, 0) * mm, "end": v(-21.16, 0) * mm});
            skLineSegment(sketch, "E106.left", {"start": v(-46.2, 5.7) * mm, "end": v(-46.2, 0) * mm});
            skLineSegment(sketch, "E106.right", {"start": v(-21.16, 5.7) * mm, "end": v(-21.16, 0) * mm});
            skLineSegment(sketch, "E107.bottom", {"start": v(-21.16, 5.7) * mm, "end": v(-26.86, 5.7) * mm});
            skLineSegment(sketch, "E107.top", {"start": v(-21.16, 34) * mm, "end": v(-26.86, 34) * mm});
            skLineSegment(sketch, "E107.left", {"start": v(-21.16, 5.7) * mm, "end": v(-21.16, 34) * mm});
            skLineSegment(sketch, "E107.right", {"start": v(-26.86, 5.7) * mm, "end": v(-26.86, 34) * mm});
            skLineSegment(sketch, "E108.bottom", {"start": v(-26.86, 34) * mm, "end": v(-39.38, 34) * mm});
            skLineSegment(sketch, "E108.top", {"start": v(-26.86, 28.3) * mm, "end": v(-39.38, 28.3) * mm});
            skLineSegment(sketch, "E108.left", {"start": v(-26.86, 34) * mm, "end": v(-26.86, 28.3) * mm});
            skLineSegment(sketch, "E108.right", {"start": v(-39.38, 34) * mm, "end": v(-39.38, 28.3) * mm});
            skLineSegment(sketch, "E109.bottom", {"start": v(-39.38, 28.3) * mm, "end": v(-33.68, 28.3) * mm});
            skLineSegment(sketch, "E109.top", {"start": v(-39.38, 5.7) * mm, "end": v(-33.68, 5.7) * mm});
            skLineSegment(sketch, "E109.left", {"start": v(-39.38, 28.3) * mm, "end": v(-39.38, 5.7) * mm});
            skLineSegment(sketch, "E109.right", {"start": v(-33.68, 28.3) * mm, "end": v(-33.68, 5.7) * mm});
            skLineSegment(sketch, "E110.bottom", {"start": v(-29.6, 34) * mm, "end": v(-35.3, 34) * mm});
            skLineSegment(sketch, "E110.top", {"start": v(-29.6, 49) * mm, "end": v(-35.3, 49) * mm});
            skLineSegment(sketch, "E110.left", {"start": v(-29.6, 34) * mm, "end": v(-29.6, 49) * mm});
            skLineSegment(sketch, "E110.right", {"start": v(-35.3, 34) * mm, "end": v(-35.3, 49) * mm});
            skLineSegment(sketch, "E111.bottom", {"start": v(-35.3, 49) * mm, "end": v(-49, 49) * mm});
            skLineSegment(sketch, "E111.top", {"start": v(-35.3, 43.3) * mm, "end": v(-49, 43.3) * mm});
            skLineSegment(sketch, "E111.left", {"start": v(-35.3, 49) * mm, "end": v(-35.3, 43.3) * mm});
            skLineSegment(sketch, "E111.right", {"start": v(-49, 49) * mm, "end": v(-49, 43.3) * mm});
            skSolve(sketch);
        }
        {
            var Q0;
            Q0=makeQuery(id+"F21.boolean.opBoolean","COPY",FACE,{"derivedFrom":makeQuery(id+"F21.opExtrude","SWEPT_FACE",FACE,{"disambiguationData":[OSD([sQuery(id+"F19.wireOp",EDGE,"E87.top")])]})});
            var sketch = newSketch(context, id + "F23", { "sketchPlane" : qUnion([Q0])});
            skCircle(sketch, "E112", {"center": v(-46.15, 46.15) * mm, "radius": 2.85 * mm});
            skCircle(sketch, "E113.MirrorC", {"center": v(-46.15, -46.15) * mm, "radius": 2.85 * mm});
            skCircle(sketch, "E114.MirrorC", {"center": v(46.15, 46.15) * mm, "radius": 2.85 * mm});
            skCircle(sketch, "E115.MirrorC", {"center": v(46.15, -46.15) * mm, "radius": 2.85 * mm});
            skSolve(sketch);
        }
        {
            var Q0;
            Q0=qSketchRegion(id+"F22",true);
            extrude(context, id + "F24", {"entities" : qUnion([Q0]), "operationType" : NewBodyOperationType.REMOVE, "oppositeDirection" : true, "depth" : 5.7 * mm});
        }
        {
            var Q0;
            Q0=qSketchRegion(id+"F23",true);
            extrude(context, id + "F25", {"entities" : qUnion([Q0]), "operationType" : NewBodyOperationType.REMOVE, "oppositeDirection" : true, "depth" : 18.4 * mm});
        }
        {
            var Q0;
            {var subQ2=sQuery(id+"F0.wireOp",EDGE,"E0.top");Q0=makeQuery(id+"F21.boolean.opBoolean","SPLIT",FACE,{"disambiguationData":[TD([makeQuery(id+"F21.opExtrude","SWEPT_FACE",FACE,{"disambiguationData":[OSD([sQuery(id+"F19.wireOp",EDGE,"E87.top")])]})])],"derivedFrom":makeQuery(id+"F12.boolean.opBoolean","SPLIT",FACE,{"disambiguationData":[TD([makeQuery(id+"F12.opExtrude","SWEPT_FACE",FACE,{"disambiguationData":[OSD([sQuery(id+"F11.wireOp",EDGE,"E41.top")])]})])],"derivedFrom":makeQuery(id+"F1.opExtrude","SWEPT_FACE",FACE,{"disambiguationData":[OSD([subQ2])]})})});}
            var sketch = newSketch(context, id + "F26", { "sketchPlane" : qUnion([Q0])});
            skLineSegment(sketch, "E116.bottom", {"start": v(-50, -25.8) * mm, "end": v(50, -25.8) * mm});
            skLineSegment(sketch, "E116.top", {"start": v(-50, -33.8) * mm, "end": v(50, -33.8) * mm});
            skLineSegment(sketch, "E116.left", {"start": v(-50, -25.8) * mm, "end": v(-50, -33.8) * mm});
            skLineSegment(sketch, "E116.right", {"start": v(50, -25.8) * mm, "end": v(50, -33.8) * mm});
            skSolve(sketch);
        }
        {
            var Q0;
            {var subQ0=sQuery(id+"F26.wireOp",EDGE,"E116.top");Q0=makeQuery(id+"F26.imprint","IMPRINT",FACE,{"disambiguationData":[TD([[makeQuery(id+"F26.imprint","IMPRINT",EDGE,{"derivedFrom":subQ0}),-1.0]])]});}
            var sketch = newSketch(context, id + "F27", { "sketchPlane" : qUnion([Q0])});
            skLineSegment(sketch, "E117.bottom", {"start": v(-50, -33.8) * mm, "end": v(50, -33.8) * mm});
            skLineSegment(sketch, "E117.top", {"start": v(-50, -38.7) * mm, "end": v(50, -38.7) * mm});
            skLineSegment(sketch, "E117.left", {"start": v(-50, -33.8) * mm, "end": v(-50, -38.7) * mm});
            skLineSegment(sketch, "E117.right", {"start": v(50, -33.8) * mm, "end": v(50, -38.7) * mm});
            skSolve(sketch);
        }
        {
            var Q0;
            Q0=qSketchRegion(id+"F27",true);
            extrude(context, id + "F28", {"entities" : qUnion([Q0]), "operationType" : NewBodyOperationType.REMOVE, "endBound" : BoundingType.THROUGH_ALL, "oppositeDirection" : true, "depth" : 25 * mm});
        }
        {
            var Q0;
            Q0=makeQuery(id+"F28.boolean.opBoolean","COPY",FACE,{"derivedFrom":makeQuery(id+"F28.opExtrude","SWEPT_FACE",FACE,{"disambiguationData":[OSD([sQuery(id+"F27.wireOp",EDGE,"E117.top")])]})});
            var sketch = newSketch(context, id + "F29", { "sketchPlane" : qUnion([Q0])});
            skLineSegment(sketch, "E118.bottom", {"start": v(-48.98, -45.8) * mm, "end": v(-43.28, -45.8) * mm});
            skLineSegment(sketch, "E118.top", {"start": v(-48.98, -18.38) * mm, "end": v(-43.28, -18.38) * mm});
            skLineSegment(sketch, "E118.left", {"start": v(-48.98, -45.8) * mm, "end": v(-48.98, -18.38) * mm});
            skLineSegment(sketch, "E118.right", {"start": v(-43.28, -45.8) * mm, "end": v(-43.28, -18.38) * mm});
            skLineSegment(sketch, "E119.bottom", {"start": v(43.33, -45.73) * mm, "end": v(49.03, -45.73) * mm});
            skLineSegment(sketch, "E119.top", {"start": v(43.33, -6.05) * mm, "end": v(49.03, -6.05) * mm});
            skLineSegment(sketch, "E119.left", {"start": v(43.33, -45.73) * mm, "end": v(43.33, -6.05) * mm});
            skLineSegment(sketch, "E119.right", {"start": v(49.03, -45.73) * mm, "end": v(49.03, -6.05) * mm});
            skLineSegment(sketch, "E120.bottom", {"start": v(49, 46.07) * mm, "end": v(43.3, 46.07) * mm});
            skLineSegment(sketch, "E120.top", {"start": v(49, 19.78) * mm, "end": v(43.3, 19.78) * mm});
            skLineSegment(sketch, "E120.left", {"start": v(49, 46.07) * mm, "end": v(49, 19.78) * mm});
            skLineSegment(sketch, "E120.right", {"start": v(43.3, 46.07) * mm, "end": v(43.3, 19.78) * mm});
            skLineSegment(sketch, "E121.bottom", {"start": v(-43.32, 45.84) * mm, "end": v(-49.02, 45.84) * mm});
            skLineSegment(sketch, "E121.top", {"start": v(-43.32, 22.18) * mm, "end": v(-49.02, 22.18) * mm});
            skLineSegment(sketch, "E121.left", {"start": v(-43.32, 45.84) * mm, "end": v(-43.32, 22.18) * mm});
            skLineSegment(sketch, "E121.right", {"start": v(-49.02, 45.84) * mm, "end": v(-49.02, 22.18) * mm});
            skLineSegment(sketch, "E122.bottom", {"start": v(-43.32, 22.18) * mm, "end": v(-34.41, 22.18) * mm});
            skLineSegment(sketch, "E122.top", {"start": v(-43.32, 27.88) * mm, "end": v(-34.41, 27.88) * mm});
            skLineSegment(sketch, "E122.left", {"start": v(-43.32, 22.18) * mm, "end": v(-43.32, 27.88) * mm});
            skLineSegment(sketch, "E122.right", {"start": v(-34.41, 22.18) * mm, "end": v(-34.41, 27.88) * mm});
            skCircle(sketch, "E123", {"center": v(-32.83, 24.91) * mm, "radius": 4.62 * mm});
            skPoint(sketch, "E123.first.point", {"position": v(-36.37, 27.88) * mm});
            skPoint(sketch, "E123.second.point", {"position": v(-36.56, 22.18) * mm});
            skPoint(sketch, "E123.third.point", {"position": v(-28.23, 25.25) * mm});
            skLineSegment(sketch, "E124.bottom", {"start": v(43.3, 19.78) * mm, "end": v(27.85, 19.78) * mm});
            skLineSegment(sketch, "E124.top", {"start": v(43.3, 25.48) * mm, "end": v(27.85, 25.48) * mm});
            skLineSegment(sketch, "E124.left", {"start": v(43.3, 19.78) * mm, "end": v(43.3, 25.48) * mm});
            skLineSegment(sketch, "E124.right", {"start": v(27.85, 19.78) * mm, "end": v(27.85, 25.48) * mm});
            skCircle(sketch, "E125", {"center": v(24.3, 22.15) * mm, "radius": 5.64 * mm});
            skPoint(sketch, "E125.first.point", {"position": v(28.86, 25.48) * mm});
            skPoint(sketch, "E125.second.point", {"position": v(29.43, 19.78) * mm});
            skPoint(sketch, "E125.third.point", {"position": v(19.2, 24.55) * mm});
            skLineSegment(sketch, "E126.bottom", {"start": v(43.33, -6.05) * mm, "end": v(37.18, -6.05) * mm});
            skLineSegment(sketch, "E126.top", {"start": v(43.33, -11.75) * mm, "end": v(37.18, -11.75) * mm});
            skLineSegment(sketch, "E126.left", {"start": v(43.33, -6.05) * mm, "end": v(43.33, -11.75) * mm});
            skLineSegment(sketch, "E126.right", {"start": v(37.18, -6.05) * mm, "end": v(37.18, -11.75) * mm});
            skCircle(sketch, "E127", {"center": v(27.07, -13.01) * mm, "radius": 13.17 * mm});
            skPoint(sketch, "E127.first.point", {"position": v(38.24, -6.05) * mm});
            skPoint(sketch, "E127.second.point", {"position": v(40.17, -11.75) * mm});
            skPoint(sketch, "E127.third.point", {"position": v(14.38, -16.52) * mm});
            skLineSegment(sketch, "E128.bottom", {"start": v(-43.28, -18.38) * mm, "end": v(-27.67, -18.38) * mm});
            skLineSegment(sketch, "E128.top", {"start": v(-43.28, -24.08) * mm, "end": v(-27.67, -24.08) * mm});
            skLineSegment(sketch, "E128.left", {"start": v(-43.28, -18.38) * mm, "end": v(-43.28, -24.08) * mm});
            skLineSegment(sketch, "E128.right", {"start": v(-27.67, -18.38) * mm, "end": v(-27.67, -24.08) * mm});
            skCircle(sketch, "E129", {"center": v(-24.83, -20.83) * mm, "radius": 5.35 * mm});
            skPoint(sketch, "E129.first.point", {"position": v(-29.59, -18.38) * mm});
            skPoint(sketch, "E129.second.point", {"position": v(-29.08, -24.08) * mm});
            skPoint(sketch, "E129.third.point", {"position": v(-19.5, -20.46) * mm});
            skLineSegment(sketch, "E130", {"start": v(-32.13, 29.48) * mm, "end": v(-19.97, 46.28) * mm});
            skLineSegment(sketch, "E131", {"start": v(-19.97, 46.28) * mm, "end": v(-15.35, 42.93) * mm});
            skLineSegment(sketch, "E132", {"start": v(-15.35, 42.93) * mm, "end": v(-28.23, 25.32) * mm});
            skLineSegment(sketch, "E133", {"start": v(-28.23, 25.32) * mm, "end": v(-32.13, 29.48) * mm});
            skLineSegment(sketch, "E134", {"start": v(23.3, 27.7) * mm, "end": v(10.2, 46.28) * mm});
            skLineSegment(sketch, "E135", {"start": v(10.2, 46.28) * mm, "end": v(5.53, 43) * mm});
            skLineSegment(sketch, "E136", {"start": v(5.53, 43) * mm, "end": v(18.97, 23.98) * mm});
            skLineSegment(sketch, "E137", {"start": v(18.97, 23.98) * mm, "end": v(23.3, 27.7) * mm});
            skLineSegment(sketch, "E138.bottom", {"start": v(-19.97, 46.28) * mm, "end": v(10.19, 46.28) * mm});
            skLineSegment(sketch, "E138.top", {"start": v(-19.97, 40.58) * mm, "end": v(10.19, 40.58) * mm});
            skLineSegment(sketch, "E138.left", {"start": v(-19.97, 46.28) * mm, "end": v(-19.97, 40.58) * mm});
            skLineSegment(sketch, "E138.right", {"start": v(10.19, 46.28) * mm, "end": v(10.19, 40.58) * mm});
            skLineSegment(sketch, "E139", {"start": v(-25.55, -26.13) * mm, "end": v(-18.32, -42.06) * mm});
            skLineSegment(sketch, "E140", {"start": v(-18.32, -42.06) * mm, "end": v(-13.13, -39.7) * mm});
            skLineSegment(sketch, "E141", {"start": v(-13.13, -39.7) * mm, "end": v(-20.36, -23.77) * mm});
            skLineSegment(sketch, "E142", {"start": v(-20.36, -23.77) * mm, "end": v(-25.55, -26.13) * mm});
            skLineSegment(sketch, "E143", {"start": v(18.37, -22.9) * mm, "end": v(6.56, -36.36) * mm});
            skLineSegment(sketch, "E144", {"start": v(6.56, -36.36) * mm, "end": v(11.55, -39.12) * mm});
            skLineSegment(sketch, "E145", {"start": v(11.55, -39.12) * mm, "end": v(23.36, -25.65) * mm});
            skLineSegment(sketch, "E146", {"start": v(23.36, -25.65) * mm, "end": v(18.37, -22.9) * mm});
            skLineSegment(sketch, "E147.bottom", {"start": v(-18.32, -42.06) * mm, "end": v(11.55, -42.06) * mm});
            skLineSegment(sketch, "E147.top", {"start": v(-18.32, -36.36) * mm, "end": v(11.55, -36.36) * mm});
            skLineSegment(sketch, "E147.left", {"start": v(-18.32, -42.06) * mm, "end": v(-18.32, -36.36) * mm});
            skLineSegment(sketch, "E147.right", {"start": v(11.55, -42.06) * mm, "end": v(11.55, -36.36) * mm});
            skLineSegment(sketch, "E148.bottom", {"start": v(-4.9, 40.58) * mm, "end": v(0.8, 40.58) * mm});
            skLineSegment(sketch, "E148.top", {"start": v(-4.9, 7.22) * mm, "end": v(0.8, 7.22) * mm});
            skLineSegment(sketch, "E148.left", {"start": v(-4.9, 40.58) * mm, "end": v(-4.9, 7.22) * mm});
            skLineSegment(sketch, "E148.right", {"start": v(0.8, 40.58) * mm, "end": v(0.8, 7.22) * mm});
            skLineSegment(sketch, "E149.bottom", {"start": v(-4.46, -36.36) * mm, "end": v(1.24, -36.36) * mm});
            skLineSegment(sketch, "E149.top", {"start": v(-4.46, -5.52) * mm, "end": v(1.24, -5.52) * mm});
            skLineSegment(sketch, "E149.left", {"start": v(-4.46, -36.36) * mm, "end": v(-4.46, -5.52) * mm});
            skLineSegment(sketch, "E149.right", {"start": v(1.24, -36.36) * mm, "end": v(1.24, -5.52) * mm});
            skSolve(sketch);
        }
        {
            var Q0;
            Q0=makeQuery(id+"F28.boolean.opBoolean","COPY",FACE,{"derivedFrom":makeQuery(id+"F28.opExtrude","SWEPT_FACE",FACE,{"disambiguationData":[OSD([sQuery(id+"F27.wireOp",EDGE,"E117.top")])]})});
            var sketch = newSketch(context, id + "F30", { "sketchPlane" : qUnion([Q0])});
            skCircle(sketch, "E150", {"center": v(-1.62, 1.05) * mm, "radius": 11.4 * mm});
            skPoint(sketch, "E150.first.point", {"position": v(-7.13, 11.03) * mm});
            skPoint(sketch, "E150.second.point", {"position": v(2.85, -9.43) * mm});
            skPoint(sketch, "E150.third.point", {"position": v(-6.37, -9.3) * mm});
            skSolve(sketch);
        }
        {
            var Q0;
            Q0=qSketchRegion(id+"F29",true);
            extrude(context, id + "F31", {"entities" : qUnion([Q0]), "operationType" : NewBodyOperationType.REMOVE, "oppositeDirection" : true, "depth" : 5.7 * mm});
        }
        {
            var Q0;
            Q0=qSketchRegion(id+"F30",true);
            extrude(context, id + "F32", {"entities" : qUnion([Q0]), "operationType" : NewBodyOperationType.REMOVE, "oppositeDirection" : true, "depth" : 7 * mm});
        }
        {
            var Q0;
            {var subQ2=sQuery(id+"F0.wireOp",EDGE,"E0.left");Q0=makeQuery(id+"F28.boolean.opBoolean","SPLIT",FACE,{"disambiguationData":[TD([makeQuery(id+"F28.opExtrude","SWEPT_FACE",FACE,{"disambiguationData":[OSD([sQuery(id+"F27.wireOp",EDGE,"E117.top")])]})])],"derivedFrom":makeQuery(id+"F21.boolean.opBoolean","SPLIT",FACE,{"disambiguationData":[TD([makeQuery(id+"F21.opExtrude","SWEPT_FACE",FACE,{"disambiguationData":[OSD([sQuery(id+"F19.wireOp",EDGE,"E87.top")])]})])],"derivedFrom":makeQuery(id+"F12.boolean.opBoolean","SPLIT",FACE,{"disambiguationData":[TD([makeQuery(id+"F12.opExtrude","SWEPT_FACE",FACE,{"disambiguationData":[OSD([sQuery(id+"F11.wireOp",EDGE,"E41.top")])]})])],"derivedFrom":makeQuery(id+"F1.opExtrude","SWEPT_FACE",FACE,{"disambiguationData":[OSD([subQ2])]})})})});}
            var sketch = newSketch(context, id + "F33", { "sketchPlane" : qUnion([Q0])});
            skLineSegment(sketch, "E151.bottom", {"start": v(-5, -43.3) * mm, "end": v(0.7, -43.3) * mm});
            skLineSegment(sketch, "E151.top", {"start": v(-5, -49) * mm, "end": v(0.7, -49) * mm});
            skLineSegment(sketch, "E151.left", {"start": v(-5, -43.3) * mm, "end": v(-5, -49) * mm});
            skLineSegment(sketch, "E151.right", {"start": v(0.7, -43.3) * mm, "end": v(0.7, -49) * mm});
            skSolve(sketch);
        }
        {
            var Q0;
            Q0=qSketchRegion(id+"F33",true);
            extrude(context, id + "F34", {"entities" : qUnion([Q0]), "operationType" : NewBodyOperationType.REMOVE, "oppositeDirection" : true, "depth" : 55 * mm});
        }
        {
            var Q0;
            Q0=qSketchRegion(id+"F7",true);
            extrude(context, id + "F35", {"entities" : qUnion([Q0]), "operationType" : NewBodyOperationType.REMOVE, "oppositeDirection" : true, "depth" : 12.9 * mm});
        }
    });
